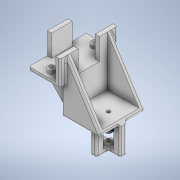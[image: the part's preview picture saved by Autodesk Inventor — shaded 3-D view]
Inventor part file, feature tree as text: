
AUTODESK INVENTOR PART (.ipt)
format: ipt  version: 2020 (Build 240168000, 168)  size: 799,232 bytes
history: native  units: in
note: dims shown in document units (in); Inventor stores cm internally (conversion verified against a paired STEP export)
features: extrude x16, sketch x16, chamfer x3, fillet x3
ambient origin geometry x8: Origin, YZ Plane, XZ Plane, XY Plane, X Axis, Y Axis, Z Axis, Center Point
bodies: Solid1 (feature_tree)
feature tree (38):
  extrude  "Extrusion1"  Depth=2.6378in
  extrude  "Extrusion2"  Depth=0.1969in
  extrude  "Extrusion6"  Depth=0.1969in
  extrude  "Extrusion8"  Depth=1.0in TaperAngle=0.0deg
  chamfer  "Chamfer1"  Distance=1.0in
  extrude  "Extrusion9"  Depth=0.3406in
  extrude  "Extrusion10"  Depth=0.1969in TaperAngle=0.0deg
  extrude  "Extrusion11"  Depth=0.1575in
  extrude  "Extrusion12"  Depth=0.1575in
  extrude  "Extrusion16"  Depth=0.2362in
  extrude  "Extrusion17"  Depth=0.2362in
  extrude  "Extrusion18"  Depth=0.1969in
  extrude  "Extrusion19"  Depth=0.1969in
  extrude  "Extrusion20"  Depth=1.2992in TaperAngle=0.0deg
  chamfer  "Chamfer2"  Distance=0.1969in
  extrude  "Extrusion21"  Depth=0.0787in
  fillet  "Fillet9"  Radius=1.811in
  fillet  "Fillet10"  Radius=0.9055in
  fillet  "Fillet11"  Radius=0.1575in
  extrude  "Extrusion22"  Depth=0.3937in TaperAngle=0.0deg
  extrude  "Extrusion23"  Depth=0.3937in
  chamfer  "Chamfer3"  Distance=0.1575in
  sketch  "Sketch1"  dims[d0=1.4331in d1=2.6378in]
  sketch  "Sketch2"  dims[d2=0.1969in d3=0.0in d4=0.1969in]
  sketch  "Sketch6"  dims[d5=0.8268in d6=0.1969in]
  sketch  "Sketch8"  dims[d7=0.8268in d8=1.0in d9=0.0in]
  sketch  "Sketch9"  dims[d26=0.1969in]
  sketch  "Sketch10"  dims[d27=0.9449in d28=1.0in d29=0.0in]
  sketch  "Sketch11"  dims[d37=0.3406in d38=0.3406in]
  sketch  "Sketch12"  dims[d39=0.3406in d40=0.1969in d41=0.0in]
  sketch  "Sketch16"  dims[d42=0.0591in d43=0.0787in d44=45.0deg d45=0.1575in]
  sketch  "Sketch17"  dims[d46=0.1575in d47=0.1575in]
  sketch  "Sketch18"  dims[d48=0.7874in d49=0.0in d50=0.2362in]
  sketch  "Sketch19"  dims[d51=0.2362in d52=0.2362in]
  sketch  "Sketch20"  dims[d53=0.0984in d54=0.0in d55=0.1969in]
  sketch  "Sketch21"  dims[d56=2.0866in d57=0.1969in]
  sketch  "Sketch22"  dims[d58=0.1969in d59=1.2992in d60=0.0in]
  sketch  "Sketch23"  dims[d61=0.1969in d62=0.1969in d63=0.1969in d64=1.811in d65=0.0in d83=0.9055in d84=0.1575in d85=0.3937in d86=0.0in d87=0.3937in d88=0.1575in d89=0.2953in d90=0.2953in d91=0.2953in d92=0.2953in d93=0.2953in d94=0.2953in d95=0.2953in d96=0.2953in d97=0.6299in d98=0.0in d99=0.6102in d100=0.0in d101=0.2953in d102=0.2953in d103=0.2953in d104=0.2953in d105=0.2953in d106=0.0in d107=0.3543in d108=0.6693in d109=0.0in d110=0.0787in d111=0.0787in d112=45.0deg d113=3.937in d114=0.0in d115=0.0787in d116=0.0787in d117=0.0787in d118=1.2402in d119=0.0in d120=0.3937in d121=0.7874in d122=0.0787in d123=0.0in d124=0.0787in d125=0.0787in d126=45.0deg d10=0.0197in d11=0.0344in d13=0.0197in d14=0.0344in d15=0.0197in d16=0.0344in d80=0.0197in d81=0.0344in d82=0.0197in]
